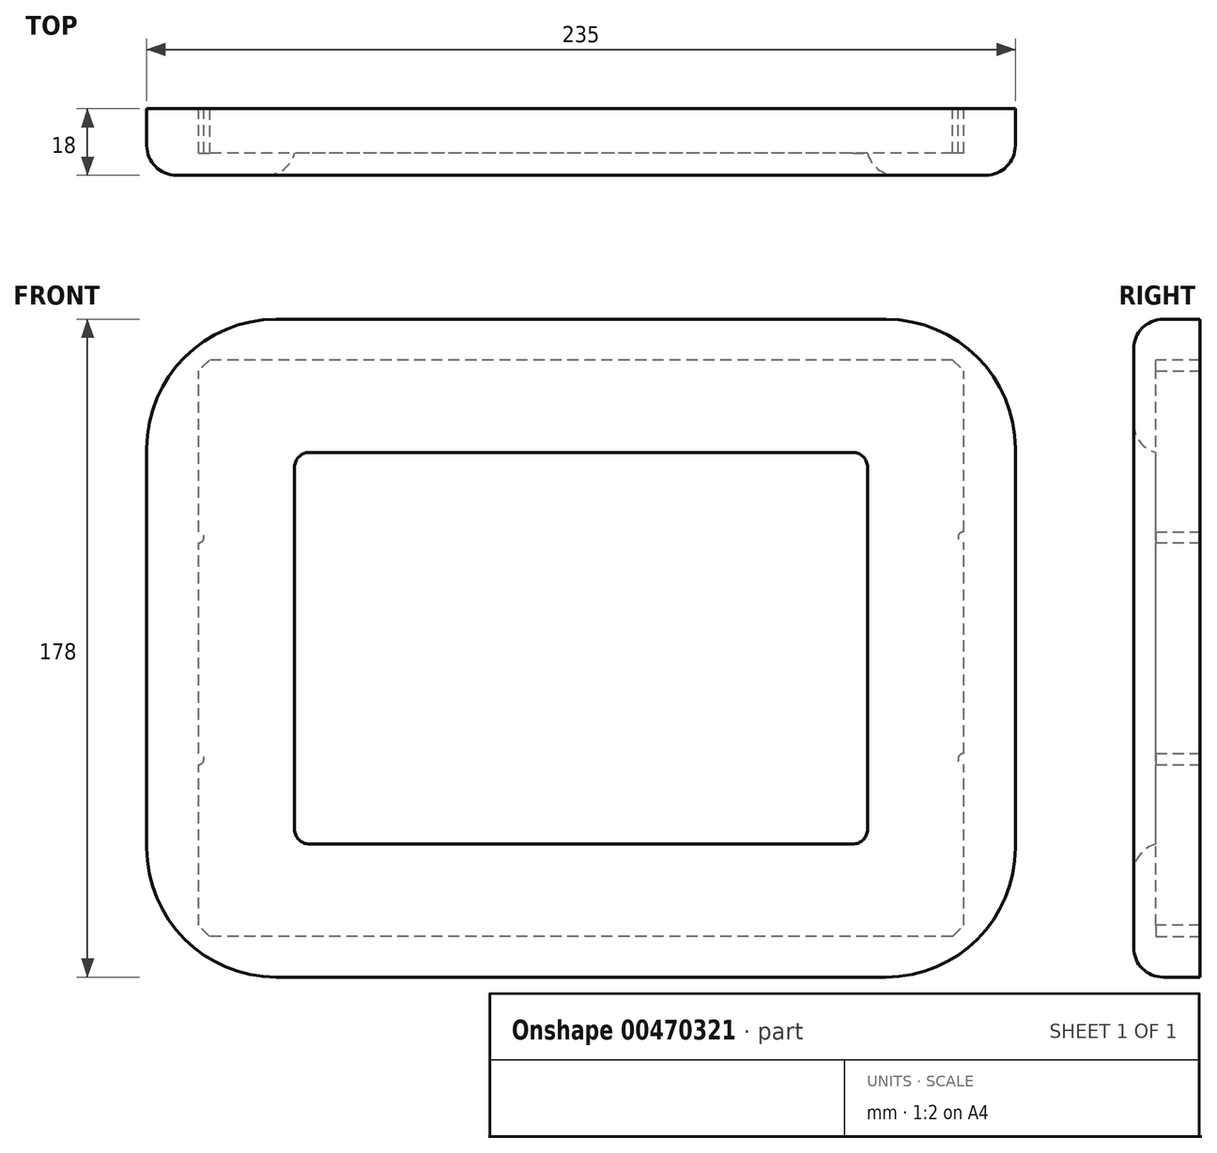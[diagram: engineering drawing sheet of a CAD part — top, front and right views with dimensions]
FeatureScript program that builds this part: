
annotation { "Feature Type Name" : "Feature", "Feature Type Description" : "" }
export const myFeature = defineFeature(function(context is Context, id is Id, definition is map)
    precondition{}
    {
        {
            var Q0;
            Q0=qCreatedBy(makeId("Front.planeOp"),FACE);
            var sketch = newSketch(context, id + "F0", { "sketchPlane" : qUnion([Q0])});
            skLineSegment(sketch, "E0.bottom", {"start": v(103.5, -78) * mm, "end": v(-103.5, -78) * mm});
            skLineSegment(sketch, "E0.top", {"start": v(103.5, 78) * mm, "end": v(-103.5, 78) * mm});
            skLineSegment(sketch, "E0.left", {"start": v(103.5, -78) * mm, "end": v(103.5, 78) * mm});
            skLineSegment(sketch, "E0.right", {"start": v(-103.5, -78) * mm, "end": v(-103.5, 78) * mm});
            skPoint(sketch, "E0.middle", {"position": v(0, 0) * mm});
            skLineSegment(sketch, "E1.bottom", {"start": v(117.5, -89) * mm, "end": v(-117.5, -89) * mm});
            skLineSegment(sketch, "E1.top", {"start": v(117.5, 89) * mm, "end": v(-117.5, 89) * mm});
            skLineSegment(sketch, "E1.left", {"start": v(117.5, -89) * mm, "end": v(117.5, 89) * mm});
            skLineSegment(sketch, "E1.right", {"start": v(-117.5, -89) * mm, "end": v(-117.5, 89) * mm});
            skLineSegment(sketch, "E2.bottom", {"start": v(77.5, -53) * mm, "end": v(-77.5, -53) * mm});
            skLineSegment(sketch, "E2.top", {"start": v(77.5, 53) * mm, "end": v(-77.5, 53) * mm});
            skLineSegment(sketch, "E2.left", {"start": v(77.5, -53) * mm, "end": v(77.5, 53) * mm});
            skLineSegment(sketch, "E2.right", {"start": v(-77.5, -53) * mm, "end": v(-77.5, 53) * mm});
            skSolve(sketch);
        }
        {
            var Q0;
            Q0=makeQuery(id+"F0.imprint","IMPRINT",FACE,{"disambiguationData":[TD([[makeQuery(id+"F0.imprint","IMPRINT",EDGE,{"derivedFrom":sQuery(id+"F0.wireOp",EDGE,"E0.bottom")}),1.0]])]});
            var Q1;
            Q1=makeQuery(id+"F0.imprint","IMPRINT",FACE,{"disambiguationData":[TD([[makeQuery(id+"F0.imprint","IMPRINT",EDGE,{"derivedFrom":sQuery(id+"F0.wireOp",EDGE,"E0.bottom")}),-1.0]])]});
            extrude(context, id + "F1", {"entities" : qUnion([Q0, Q1]), "depth" : 18 * mm});
        }
        {
            var Q0;
            Q0=makeQuery(id+"F0.imprint","IMPRINT",FACE,{"disambiguationData":[TD([[makeQuery(id+"F0.imprint","IMPRINT",EDGE,{"derivedFrom":sQuery(id+"F0.wireOp",EDGE,"E0.bottom")}),-1.0]])]});
            extrude(context, id + "F2", {"entities" : qUnion([Q0]), "operationType" : NewBodyOperationType.REMOVE, "depth" : 12 * mm});
        }
        {
            var Q0;
            Q0=makeQuery(id+"F1.opExtrude","SWEPT_EDGE",EDGE,{"disambiguationData":[OSD([sQuery(id+"F0.wireOp",EDGE,"E1.top"),sQuery(id+"F0.wireOp",EDGE,"E1.left")])]});
            var Q1;
            Q1=makeQuery(id+"F1.opExtrude","SWEPT_EDGE",EDGE,{"disambiguationData":[OSD([sQuery(id+"F0.wireOp",EDGE,"E1.top"),sQuery(id+"F0.wireOp",EDGE,"E1.right")])]});
            var Q2;
            Q2=makeQuery(id+"F1.opExtrude","SWEPT_EDGE",EDGE,{"disambiguationData":[OSD([sQuery(id+"F0.wireOp",EDGE,"E1.bottom"),sQuery(id+"F0.wireOp",EDGE,"E1.left")])]});
            var Q3;
            Q3=makeQuery(id+"F1.opExtrude","SWEPT_EDGE",EDGE,{"disambiguationData":[OSD([sQuery(id+"F0.wireOp",EDGE,"E1.bottom"),sQuery(id+"F0.wireOp",EDGE,"E1.right")])]});
            fillet(context, id + "F3", {"entities" : qUnion([Q0, Q1, Q2, Q3]), "radius" : 35 * mm, "tangentPropagation" : true, "allowEdgeOverflow" : false});
        }
        {
            var Q0;
            Q0=makeQuery(id+"F1.opExtrude","SWEPT_EDGE",EDGE,{"disambiguationData":[OSD([sQuery(id+"F0.wireOp",EDGE,"E2.top"),sQuery(id+"F0.wireOp",EDGE,"E2.right")])]});
            var Q1;
            Q1=makeQuery(id+"F1.opExtrude","SWEPT_EDGE",EDGE,{"disambiguationData":[OSD([sQuery(id+"F0.wireOp",EDGE,"E2.top"),sQuery(id+"F0.wireOp",EDGE,"E2.left")])]});
            var Q2;
            Q2=makeQuery(id+"F1.opExtrude","SWEPT_EDGE",EDGE,{"disambiguationData":[OSD([sQuery(id+"F0.wireOp",EDGE,"E2.bottom"),sQuery(id+"F0.wireOp",EDGE,"E2.left")])]});
            var Q3;
            Q3=makeQuery(id+"F1.opExtrude","SWEPT_EDGE",EDGE,{"disambiguationData":[OSD([sQuery(id+"F0.wireOp",EDGE,"E2.bottom"),sQuery(id+"F0.wireOp",EDGE,"E2.right")])]});
            fillet(context, id + "F4", {"entities" : qUnion([Q0, Q1, Q2, Q3]), "radius" : 4 * mm, "tangentPropagation" : true, "allowEdgeOverflow" : false});
        }
        {
            var Q0;
            Q0=makeQuery(id+"F1.opExtrude","CAP_FACE",FACE,{"disambiguationData":[OSD([sQuery(id+"F0.wireOp",EDGE,"E1.bottom"),sQuery(id+"F0.wireOp",EDGE,"E1.top"),sQuery(id+"F0.wireOp",EDGE,"E1.left"),sQuery(id+"F0.wireOp",EDGE,"E1.right"),sQuery(id+"F0.wireOp",EDGE,"E2.bottom"),sQuery(id+"F0.wireOp",EDGE,"E2.top"),sQuery(id+"F0.wireOp",EDGE,"E2.left"),sQuery(id+"F0.wireOp",EDGE,"E2.right")])],"isStart":false});
            fillet(context, id + "F5", {"entities" : qUnion([Q0]), "radius" : 8 * mm, "tangentPropagation" : true, "allowEdgeOverflow" : false});
        }
        {
            var Q0;
            Q0=makeQuery(id+"F2.boolean.opBoolean","COPY",EDGE,{"derivedFrom":makeQuery(id+"F2.opExtrude","SWEPT_EDGE",EDGE,{"disambiguationData":[OSD([sQuery(id+"F0.wireOp",EDGE,"E0.bottom"),sQuery(id+"F0.wireOp",EDGE,"E0.right")])]})});
            var Q1;
            Q1=makeQuery(id+"F2.boolean.opBoolean","COPY",EDGE,{"derivedFrom":makeQuery(id+"F2.opExtrude","SWEPT_EDGE",EDGE,{"disambiguationData":[OSD([sQuery(id+"F0.wireOp",EDGE,"E0.bottom"),sQuery(id+"F0.wireOp",EDGE,"E0.left")])]})});
            var Q2;
            Q2=makeQuery(id+"F2.boolean.opBoolean","COPY",EDGE,{"derivedFrom":makeQuery(id+"F2.opExtrude","SWEPT_EDGE",EDGE,{"disambiguationData":[OSD([sQuery(id+"F0.wireOp",EDGE,"E0.top"),sQuery(id+"F0.wireOp",EDGE,"E0.right")])]})});
            var Q3;
            Q3=makeQuery(id+"F2.boolean.opBoolean","COPY",EDGE,{"derivedFrom":makeQuery(id+"F2.opExtrude","SWEPT_EDGE",EDGE,{"disambiguationData":[OSD([sQuery(id+"F0.wireOp",EDGE,"E0.top"),sQuery(id+"F0.wireOp",EDGE,"E0.left")])]})});
            chamfer(context, id + "F6", {"entities" : qUnion([Q0, Q1, Q2, Q3]), "width" : 3 * mm, "tangentPropagation" : true});
        }
        {
            var Q0;
            Q0=makeQuery(id+"F0.imprint","IMPRINT",FACE,{"disambiguationData":[TD([[makeQuery(id+"F0.imprint","IMPRINT",EDGE,{"derivedFrom":sQuery(id+"F0.wireOp",EDGE,"E2.bottom")}),-1.0]])]});
            var sketch = newSketch(context, id + "F7", { "sketchPlane" : qUnion([Q0])});
            skCircle(sketch, "E3", {"center": v(-103.5, -30) * mm, "radius": 1.5 * mm});
            skCircle(sketch, "E4", {"center": v(-103.5, 30) * mm, "radius": 1.5 * mm});
            skCircle(sketch, "E5", {"center": v(103.5, -30) * mm, "radius": 1.5 * mm});
            skCircle(sketch, "E6", {"center": v(103.5, 30) * mm, "radius": 1.5 * mm});
            skSolve(sketch);
        }
        {
            var Q0;
            Q0 = qSketchRegion(id + "F7", true);
            extrude(context, id + "F8", {"entities" : qUnion([Q0]), "operationType" : NewBodyOperationType.ADD, "depth" : 16 * mm});
        }
    });
